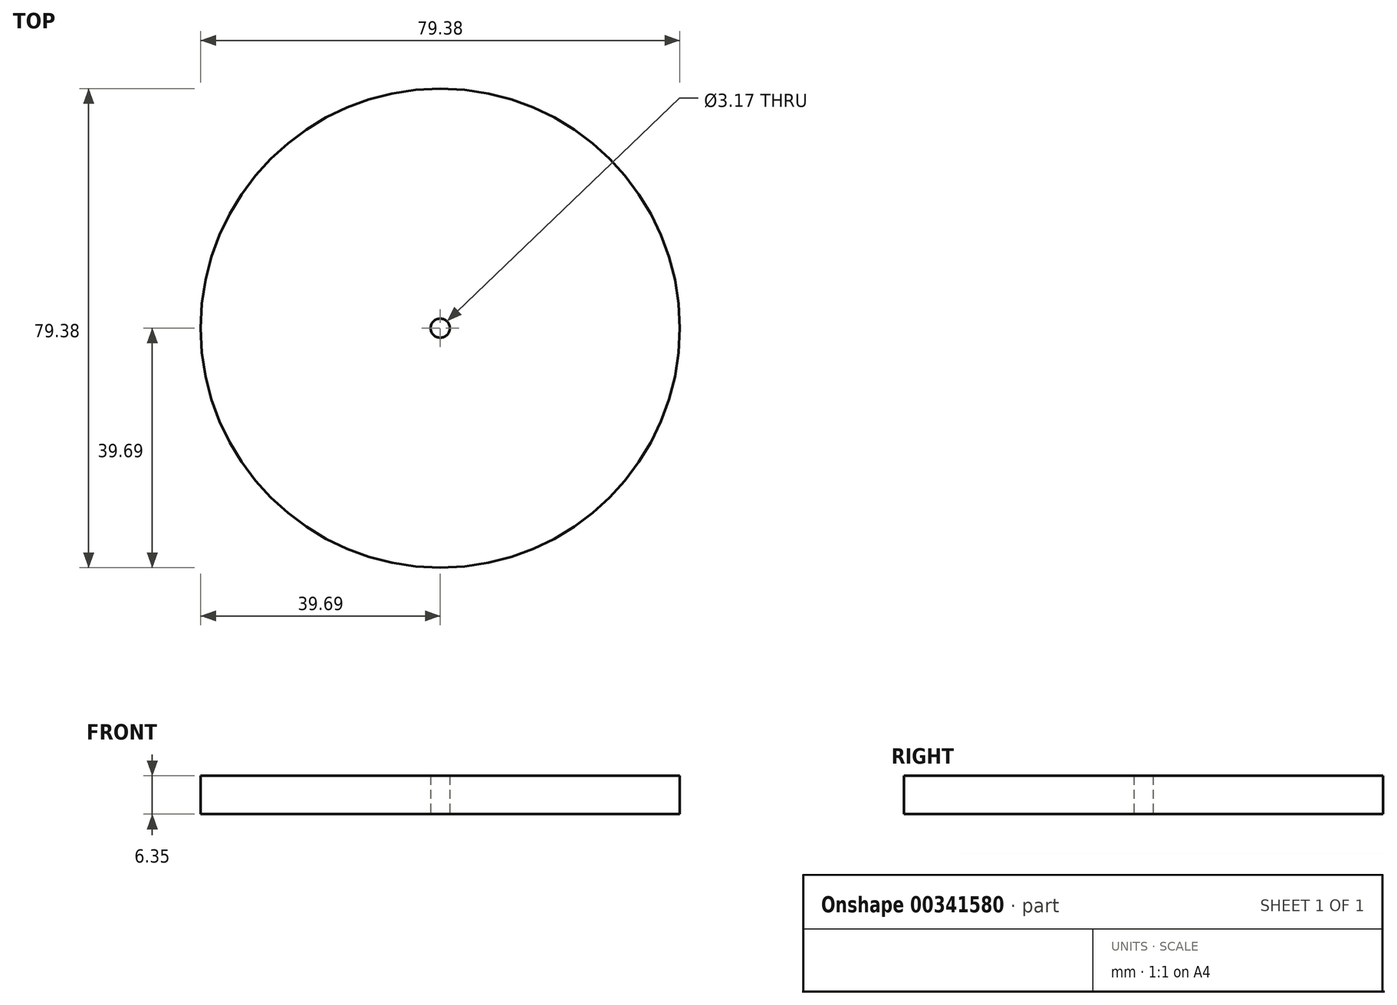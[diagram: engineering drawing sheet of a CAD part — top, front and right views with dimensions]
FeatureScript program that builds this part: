
annotation { "Feature Type Name" : "Feature", "Feature Type Description" : "" }
export const myFeature = defineFeature(function(context is Context, id is Id, definition is map)
    precondition{}
    {
        {
            var Q0;
            Q0=qCreatedBy(makeId("Top.planeOp"),FACE);
            var sketch = newSketch(context, id + "F0", { "sketchPlane" : qUnion([Q0])});
            skCircle(sketch, "E0", {"center": v(0, 0) * mm, "radius": 39.69 * mm});
            skCircle(sketch, "E1", {"center": v(0, 0) * mm, "radius": 1.59 * mm});
            skSolve(sketch);
        }
        {
            var Q0;
            Q0 = qSketchRegion(id + "F0", true);
            extrude(context, id + "F1", {"entities" : qUnion([Q0]), "depth" : 6.35 * mm});
        }
    });
